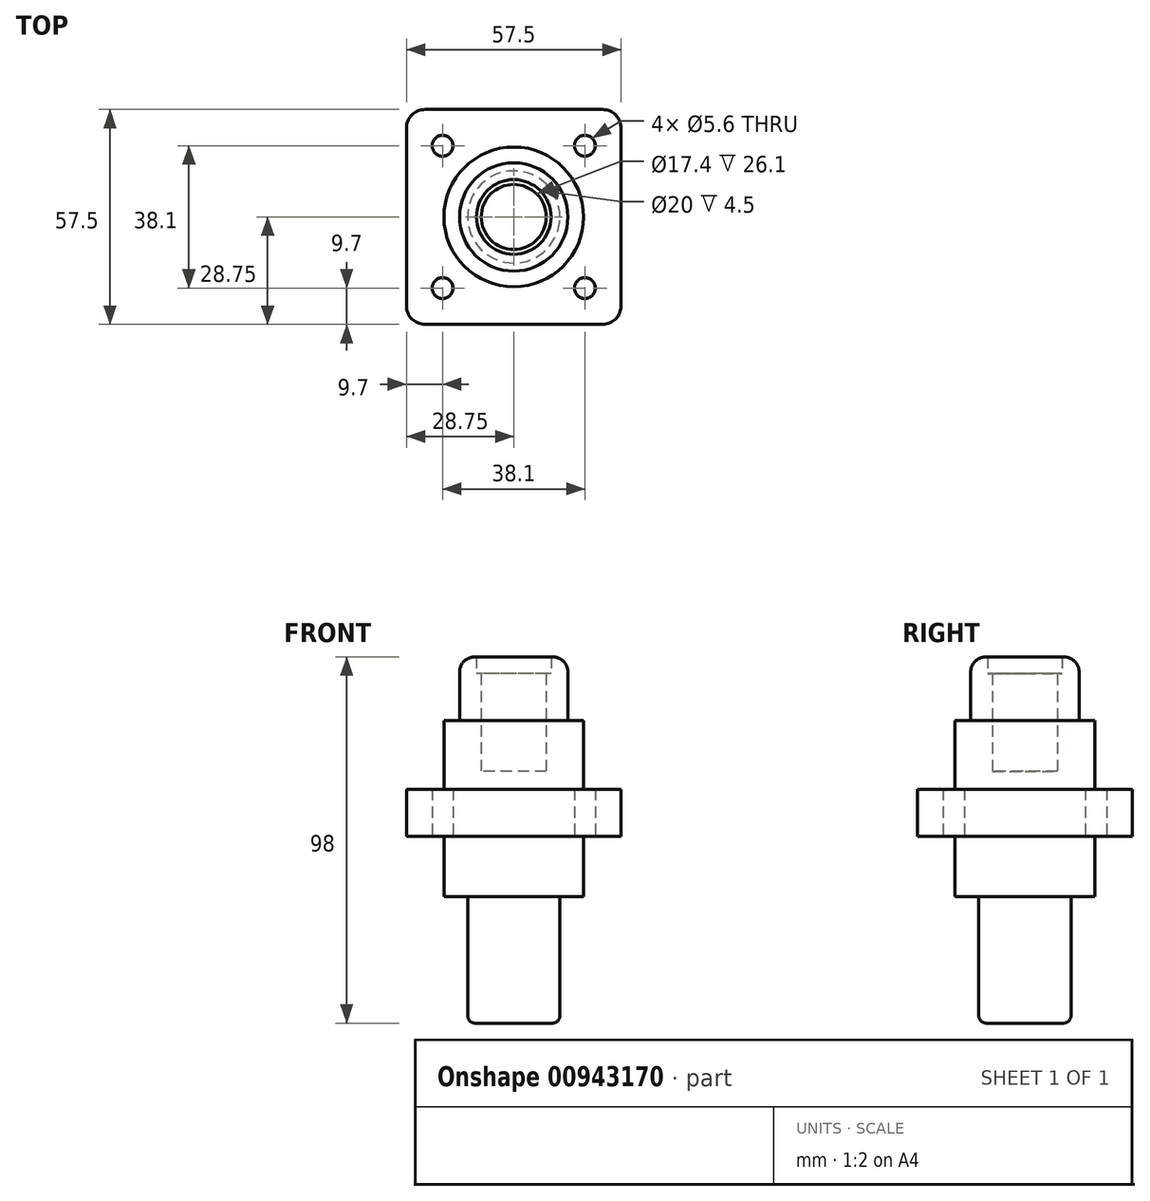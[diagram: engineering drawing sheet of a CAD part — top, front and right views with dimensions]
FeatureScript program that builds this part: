
annotation { "Feature Type Name" : "Feature", "Feature Type Description" : "" }
export const myFeature = defineFeature(function(context is Context, id is Id, definition is map)
    precondition{}
    {
        {
            var Q0;
            Q0=qCreatedBy(makeId("Top.planeOp"),FACE);
            var sketch = newSketch(context, id + "F0", { "sketchPlane" : qUnion([Q0])});
            skLineSegment(sketch, "E0.bottom", {"start": v(28.75, -28.75) * mm, "end": v(-28.75, -28.75) * mm});
            skLineSegment(sketch, "E0.top", {"start": v(28.75, 28.75) * mm, "end": v(-28.75, 28.75) * mm});
            skLineSegment(sketch, "E0.left", {"start": v(28.75, -28.75) * mm, "end": v(28.75, 28.75) * mm});
            skLineSegment(sketch, "E0.right", {"start": v(-28.75, -28.75) * mm, "end": v(-28.75, 28.75) * mm});
            skPoint(sketch, "E0.middle", {"position": v(0, 0) * mm});
            skCircle(sketch, "E1", {"center": v(0, 0) * mm, "radius": 18.7 * mm});
            skCircle(sketch, "E2", {"center": v(0, 0) * mm, "radius": 14.5 * mm});
            skCircle(sketch, "E3", {"center": v(-19.05, 19.05) * mm, "radius": 2.8 * mm});
            skCircle(sketch, "E4", {"center": v(19.05, 19.05) * mm, "radius": 2.8 * mm});
            skCircle(sketch, "E5.MirrorC", {"center": v(-19.05, -19.05) * mm, "radius": 2.8 * mm});
            skCircle(sketch, "E6.MirrorC", {"center": v(19.05, -19.05) * mm, "radius": 2.8 * mm});
            skCircle(sketch, "E7", {"center": v(0, 0) * mm, "radius": 10 * mm});
            skCircle(sketch, "E8", {"center": v(0, 0) * mm, "radius": 8.7 * mm});
            skSolve(sketch);
        }
        {
            var Q0;
            Q0 = qSketchRegion(id + "F0", true);
            extrude(context, id + "F1", {"entities" : qUnion([Q0]), "depth" : 12.6 * mm, "offsetDistance" : 25 * mm});
        }
        {
            var Q0;
            Q0=makeQuery(id+"F0.imprint","IMPRINT",FACE,{"disambiguationData":[TD([[makeQuery(id+"F0.imprint","IMPRINT",EDGE,{"derivedFrom":sQuery(id+"F0.wireOp",EDGE,"E1")}),1.0]])]});
            extrude(context, id + "F2", {"entities" : qUnion([Q0]), "operationType" : NewBodyOperationType.ADD, "depth" : 31 * mm, "offsetDistance" : 25 * mm});
        }
        {
            var Q0;
            Q0=makeQuery(id+"F0.imprint","IMPRINT",FACE,{"disambiguationData":[TD([[makeQuery(id+"F0.imprint","IMPRINT",EDGE,{"derivedFrom":sQuery(id+"F0.wireOp",EDGE,"E2")}),1.0]])]});
            extrude(context, id + "F3", {"entities" : qUnion([Q0]), "operationType" : NewBodyOperationType.ADD, "depth" : 48 * mm, "offsetDistance" : 25 * mm});
        }
        {
            var Q0;
            Q0=makeQuery(id+"F0.imprint","IMPRINT",FACE,{"disambiguationData":[TD([[makeQuery(id+"F0.imprint","IMPRINT",EDGE,{"derivedFrom":sQuery(id+"F0.wireOp",EDGE,"E7")}),1.0]])]});
            extrude(context, id + "F4", {"entities" : qUnion([Q0]), "depth" : 43.5 * mm, "offsetDistance" : 25 * mm});
        }
        {
            var Q0;
            Q0=makeQuery(id+"F0.imprint","IMPRINT",FACE,{"disambiguationData":[TD([[makeQuery(id+"F0.imprint","IMPRINT",EDGE,{"derivedFrom":sQuery(id+"F0.wireOp",EDGE,"E8")}),1.0]])]});
            extrude(context, id + "F5", {"entities" : qUnion([Q0]), "operationType" : NewBodyOperationType.ADD, "depth" : 17.4 * mm, "offsetDistance" : 25 * mm});
        }
        {
            var Q0;
            Q0=makeQuery(id+"F3.opExtrude","CAP_EDGE",EDGE,{"disambiguationData":[OSD([sQuery(id+"F0.wireOp",EDGE,"E2")])],"isStart":false});
            fillet(context, id + "F6", {"entities" : qUnion([Q0]), "radius" : 4 * mm, "tangentPropagation" : true, "allowEdgeOverflow" : false});
        }
        {
            var Q0;
            Q0=makeQuery(id+"F1.opExtrude","SWEPT_EDGE",EDGE,{"disambiguationData":[OSD([sQuery(id+"F0.wireOp",EDGE,"E0.bottom"),sQuery(id+"F0.wireOp",EDGE,"E0.right")])]});
            var Q1;
            Q1=makeQuery(id+"F1.opExtrude","SWEPT_EDGE",EDGE,{"disambiguationData":[OSD([sQuery(id+"F0.wireOp",EDGE,"E0.bottom"),sQuery(id+"F0.wireOp",EDGE,"E0.left")])]});
            var Q2;
            Q2=makeQuery(id+"F1.opExtrude","SWEPT_EDGE",EDGE,{"disambiguationData":[OSD([sQuery(id+"F0.wireOp",EDGE,"E0.top"),sQuery(id+"F0.wireOp",EDGE,"E0.left")])]});
            var Q3;
            Q3=makeQuery(id+"F1.opExtrude","SWEPT_EDGE",EDGE,{"disambiguationData":[OSD([sQuery(id+"F0.wireOp",EDGE,"E0.top"),sQuery(id+"F0.wireOp",EDGE,"E0.right")])]});
            fillet(context, id + "F7", {"entities" : qUnion([Q0, Q1, Q2, Q3]), "radius" : 5 * mm, "tangentPropagation" : true, "allowEdgeOverflow" : false});
        }
        {
            var Q0;
            Q0=makeQuery(id+"F0.imprint","IMPRINT",FACE,{"disambiguationData":[TD([[makeQuery(id+"F0.imprint","IMPRINT",EDGE,{"derivedFrom":sQuery(id+"F0.wireOp",EDGE,"E0.bottom")}),-1.0]])]});
            var sketch = newSketch(context, id + "F8", { "sketchPlane" : qUnion([Q0])});
            skCircle(sketch, "E9", {"center": v(0, 0) * mm, "radius": 18.7 * mm});
            skCircle(sketch, "E10", {"center": v(0, 0) * mm, "radius": 12.35 * mm});
            skSolve(sketch);
        }
        {
            var Q0;
            Q0=makeQuery(id+"F8.imprint","IMPRINT",FACE,{"disambiguationData":[TD([[makeQuery(id+"F8.imprint","IMPRINT",EDGE,{"derivedFrom":sQuery(id+"F8.wireOp",EDGE,"E10")}),1.0]])]});
            extrude(context, id + "F9", {"entities" : qUnion([Q0]), "oppositeDirection" : true, "depth" : 50 * mm, "offsetDistance" : 25 * mm});
        }
        {
            var Q0;
            Q0 = qSketchRegion(id + "F8", true);
            extrude(context, id + "F10", {"entities" : qUnion([Q0]), "operationType" : NewBodyOperationType.ADD, "oppositeDirection" : true, "depth" : 16.2 * mm, "offsetDistance" : 25 * mm});
        }
        {
            var Q0;
            Q0=makeQuery(id+"F9.opExtrude","CAP_EDGE",EDGE,{"disambiguationData":[OSD([sQuery(id+"F8.wireOp",EDGE,"E10")])],"isStart":false});
            fillet(context, id + "F11", {"entities" : qUnion([Q0]), "radius" : 2 * mm, "tangentPropagation" : true, "allowEdgeOverflow" : false});
        }
    });
